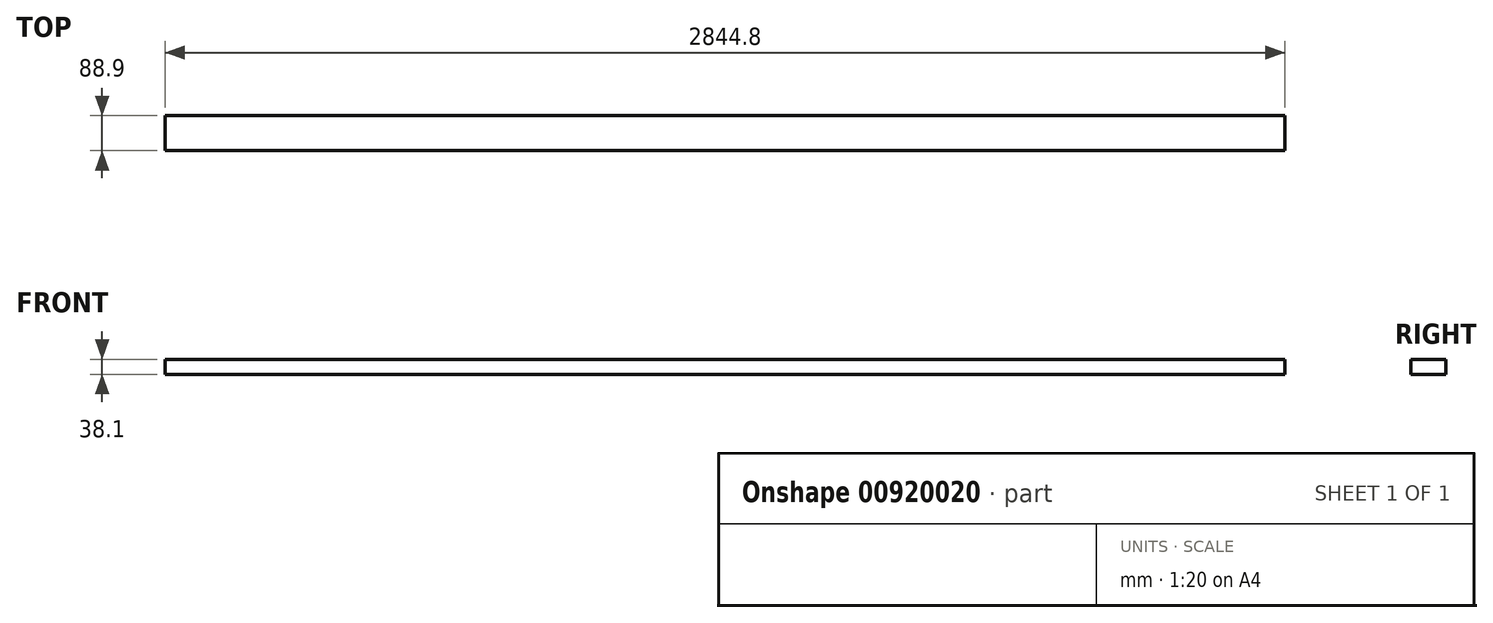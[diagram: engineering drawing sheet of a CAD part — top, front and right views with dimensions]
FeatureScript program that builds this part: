
annotation { "Feature Type Name" : "Feature", "Feature Type Description" : "" }
export const myFeature = defineFeature(function(context is Context, id is Id, definition is map)
    precondition{}
    {
        {
            var Q0;
            Q0=qCreatedBy(makeId("Right.planeOp"),FACE);
            var sketch = newSketch(context, id + "F0", { "sketchPlane" : qUnion([Q0])});
            skLineSegment(sketch, "E0.bottom", {"start": v(44.45, 19.05) * mm, "end": v(-44.45, 19.05) * mm});
            skLineSegment(sketch, "E0.top", {"start": v(44.45, -19.05) * mm, "end": v(-44.45, -19.05) * mm});
            skLineSegment(sketch, "E0.left", {"start": v(44.45, 19.05) * mm, "end": v(44.45, -19.05) * mm});
            skLineSegment(sketch, "E0.right", {"start": v(-44.45, 19.05) * mm, "end": v(-44.45, -19.05) * mm});
            skPoint(sketch, "E0.middle", {"position": v(0, 0) * mm});
            skSolve(sketch);
        }
        {
            var Q0;
            Q0=qSketchRegion(id+"F0",true);
            extrude(context, id + "F1", {"entities" : qUnion([Q0]), "oppositeDirection" : true, "depth" : 2844.8 * mm, "offsetDistance" : 25.4 * mm});
        }
    });
